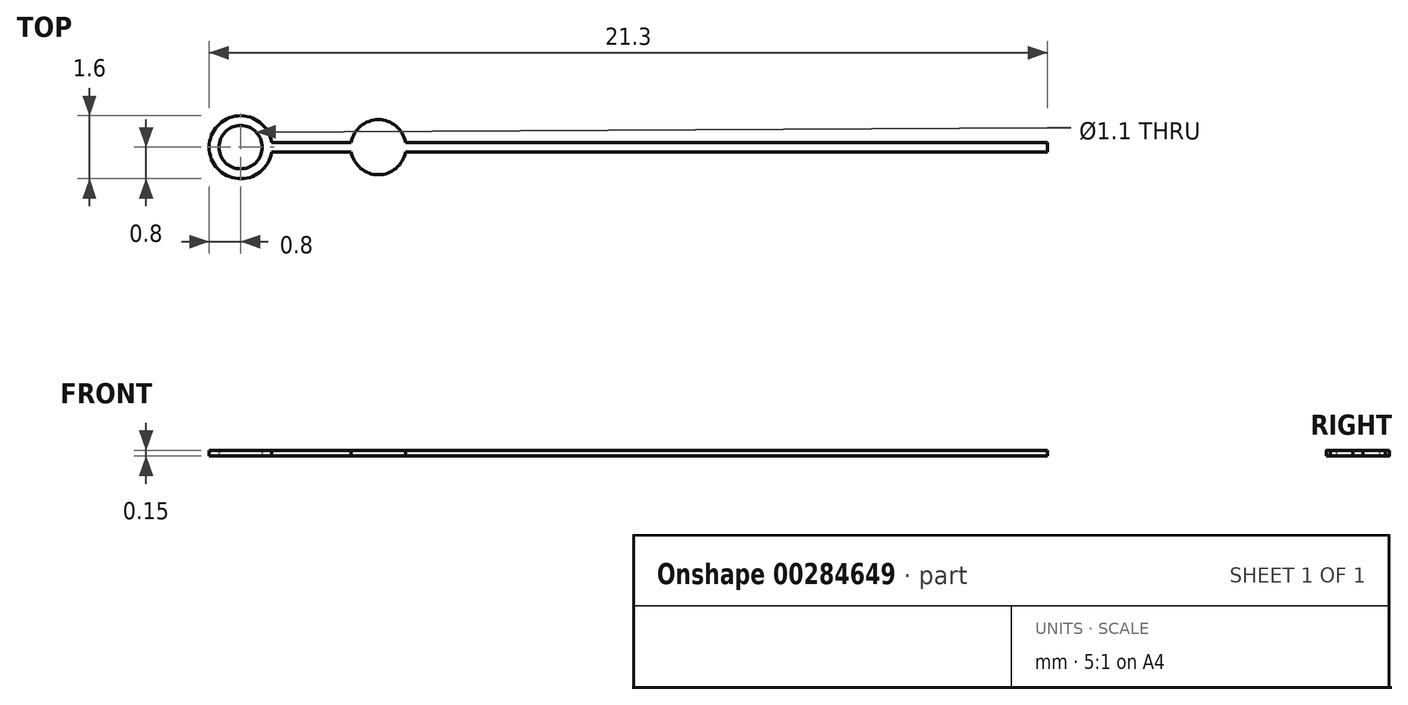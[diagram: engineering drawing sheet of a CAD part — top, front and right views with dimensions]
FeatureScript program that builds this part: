
annotation { "Feature Type Name" : "Feature", "Feature Type Description" : "" }
export const myFeature = defineFeature(function(context is Context, id is Id, definition is map)
    precondition{}
    {
        {
            var Q0;
            Q0=qCreatedBy(makeId("Top.planeOp"),FACE);
            var sketch = newSketch(context, id + "F0", { "sketchPlane" : qUnion([Q0])});
            skArc(sketch, "E0", {"start": v(-0.69, -0.12) * mm, "mid": v(0, -0.7) * mm, "end": v(0.69, -0.13) * mm});
            skLineSegment(sketch, "E1", {"start": v(0, 0) * mm, "end": v(16.5, 0) * mm, "construction": true});
            skLineSegment(sketch, "E2.0", {"start": v(-2.7, -0.12) * mm, "end": v(-0.69, -0.12) * mm});
            skLineSegment(sketch, "E3", {"start": v(0, 0) * mm, "end": v(-3.5, 0) * mm, "construction": true});
            skArc(sketch, "E4", {"start": v(-2.7, 0.12) * mm, "mid": v(-4.3, 0) * mm, "end": v(-2.7, -0.13) * mm});
            skCircle(sketch, "E5", {"center": v(-3.5, 0) * mm, "radius": 0.55 * mm});
            skArc(sketch, "E6.trimOffspring", {"start": v(0.69, 0.13) * mm, "mid": v(0, 0.7) * mm, "end": v(-0.69, 0.12) * mm});
            skLineSegment(sketch, "E7.MirrorCS", {"start": v(-2.7, 0.12) * mm, "end": v(-0.69, 0.12) * mm});
            skLineSegment(sketch, "E8", {"start": v(17, 0.12) * mm, "end": v(17, -0.12) * mm});
            skLineSegment(sketch, "E9.trimOffspring", {"start": v(0.69, 0.12) * mm, "end": v(17, 0.12) * mm});
            skLineSegment(sketch, "E10.trimOffspring", {"start": v(0.69, -0.12) * mm, "end": v(17, -0.12) * mm});
            skSolve(sketch);
        }
        {
            var Q0;
            Q0 = qSketchRegion(id + "F0", true);
            extrude(context, id + "F1", {"entities" : qUnion([Q0]), "depth" : 0.15 * mm, "offsetDistance" : 25 * mm});
        }
    });
